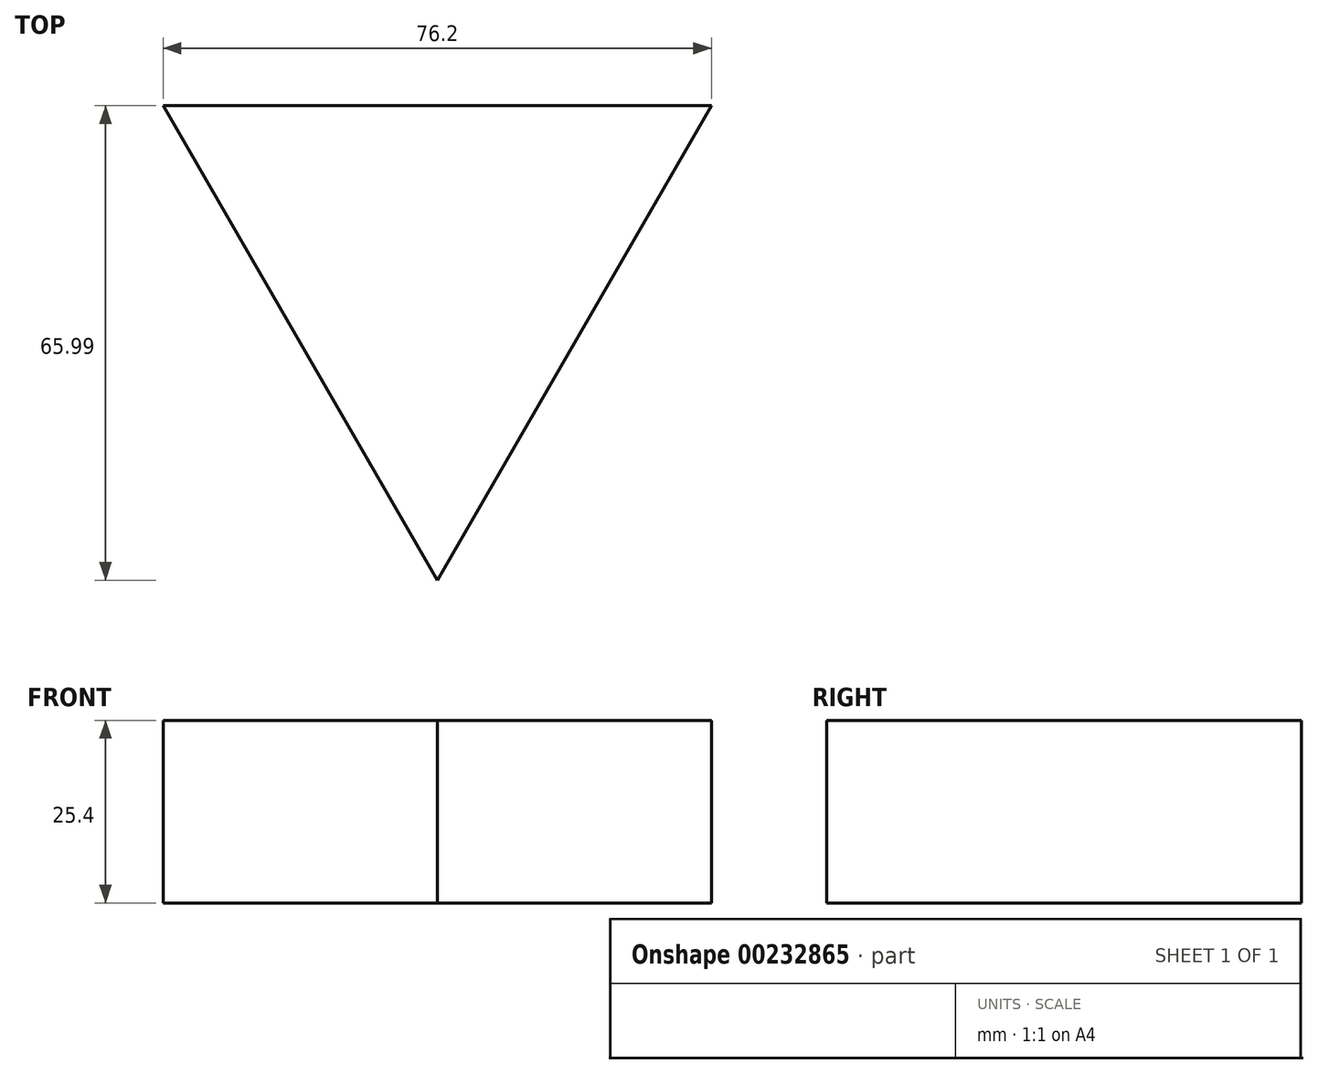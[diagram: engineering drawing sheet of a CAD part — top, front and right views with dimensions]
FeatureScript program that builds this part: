
annotation { "Feature Type Name" : "Feature", "Feature Type Description" : "" }
export const myFeature = defineFeature(function(context is Context, id is Id, definition is map)
    precondition{}
    {
        {
            var Q0;
            Q0=qCreatedBy(makeId("Top.planeOp"),FACE);
            var sketch = newSketch(context, id + "F0", { "sketchPlane" : qUnion([Q0])});
            skLineSegment(sketch, "E0", {"start": v(-39.34, 43.38) * mm, "end": v(36.86, 43.38) * mm});
            skLineSegment(sketch, "E1", {"start": v(36.86, 43.38) * mm, "end": v(-1.24, -22.61) * mm});
            skLineSegment(sketch, "E2", {"start": v(-39.34, 43.38) * mm, "end": v(-1.24, -22.61) * mm});
            skSolve(sketch);
        }
        {
            var Q0;
            Q0=makeQuery(id+"F0.imprint","IMPRINT",FACE,{"disambiguationData":[TD([[makeQuery(id+"F0.imprint","IMPRINT",EDGE,{"derivedFrom":sQuery(id+"F0.wireOp",EDGE,"E0")}),-1.0]])]});
            extrude(context, id + "F1", {"entities" : qUnion([Q0]), "depth" : 25.4 * mm});
        }
    });
